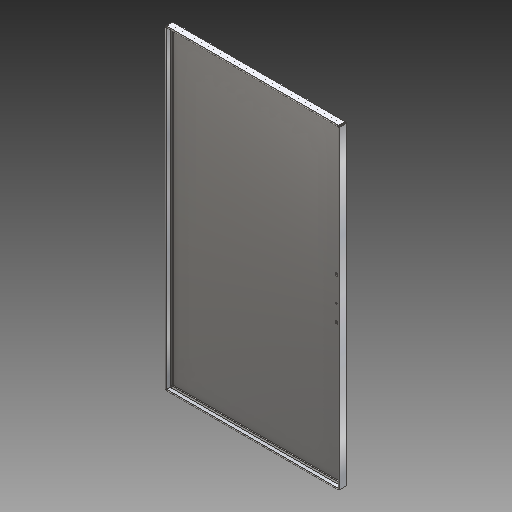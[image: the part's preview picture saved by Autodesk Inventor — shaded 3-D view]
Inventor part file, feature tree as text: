
AUTODESK INVENTOR PART (.ipt)
format: ipt  version: 2017 (Build 210142000, 142)  size: 310,784 bytes
history: native  units: in
note: dims shown in document units (in); Inventor stores cm internally (conversion verified against a paired STEP export)
features: sketch x11, other x5, plane x2, extrude x1, projected_geometry x1
ambient origin geometry x8: Origin, YZ Plane, XZ Plane, XY Plane, X Axis, Y Axis, Z Axis, Center Point
bodies: Solid1 (feature_tree)
feature tree (20):
  other  "Porta.ipt"
  extrude  "Extrusion2"  Depth=0.3937in
  plane  "Work Plane2"
  other  "Decal1"
  other  "Solid1::Porta.ipt"
  other  "TaggingFeature1"
  sketch  "Sketch1"  dims[d0=0.3937in d3=0.12in]
  sketch  "Sketch2"  dims[d4=0.0in]
  sketch  "Sketch3"  dims[d5=7.874in]
  sketch  "Sketch4"
  sketch  "Sketch5"
  sketch  "Sketch6"
  sketch  "Sketch7"
  sketch  "Sketch8"
  sketch  "Sketch9"
  plane  "Work Plane1"
  sketch  "Sketch11"
  projected_geometry  "Projected Loop1"
  sketch  "Sketch12"
  other  "Image1"
